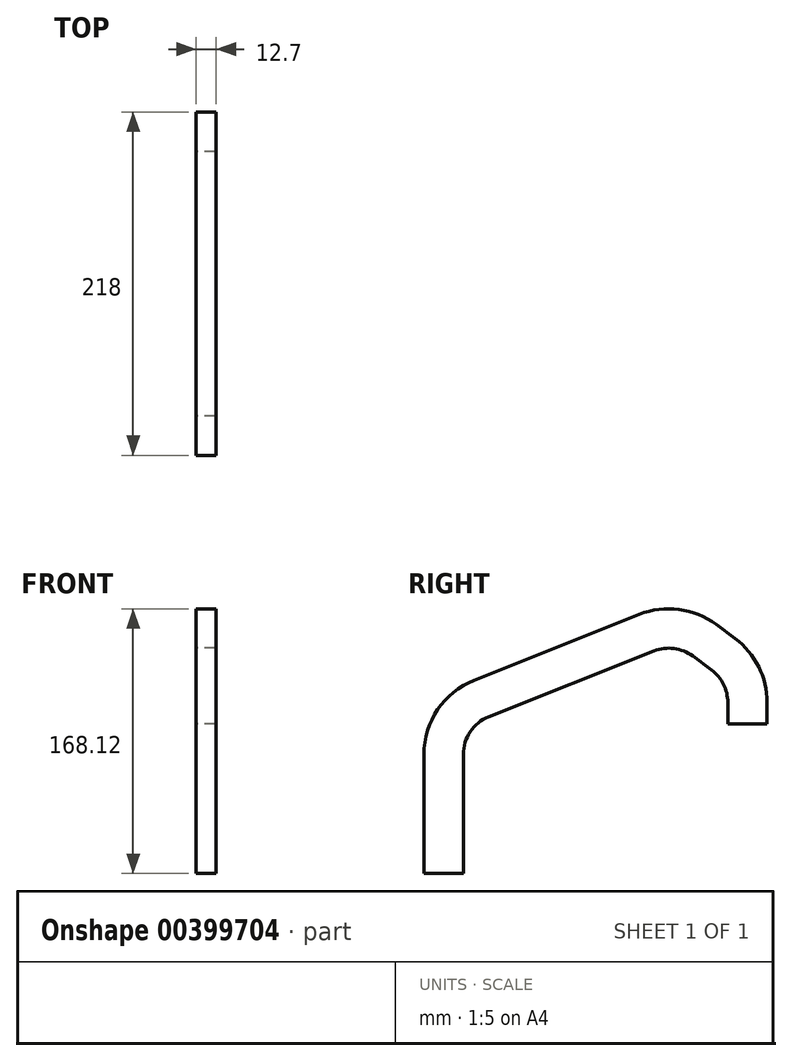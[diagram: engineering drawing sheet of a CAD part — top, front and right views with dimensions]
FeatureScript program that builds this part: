
annotation { "Feature Type Name" : "Feature", "Feature Type Description" : "" }
export const myFeature = defineFeature(function(context is Context, id is Id, definition is map)
    precondition{}
    {
        {
            var Q0;
            Q0=qCreatedBy(makeId("Right.planeOp"),FACE);
            var sketch = newSketch(context, id + "F0", { "sketchPlane" : qUnion([Q0])});
            skLineSegment(sketch, "E0", {"start": v(-159.27, -36.6) * mm, "end": v(-159.27, -146.6) * mm});
            skLineSegment(sketch, "E1", {"start": v(-159.27, -146.6) * mm, "end": v(-134.27, -146.6) * mm});
            skLineSegment(sketch, "E2", {"start": v(-134.27, -146.6) * mm, "end": v(-134.27, -53.54) * mm});
            skLineSegment(sketch, "E3", {"start": v(-134.27, -53.54) * mm, "end": v(0, 0) * mm});
            skLineSegment(sketch, "E4", {"start": v(0, 0) * mm, "end": v(33.73, -25.14) * mm});
            skLineSegment(sketch, "E5", {"start": v(33.73, -25.14) * mm, "end": v(33.73, -51.6) * mm});
            skLineSegment(sketch, "E6", {"start": v(33.73, -51.6) * mm, "end": v(58.73, -51.6) * mm});
            skLineSegment(sketch, "E7", {"start": v(58.73, -51.6) * mm, "end": v(58.73, -12.6) * mm});
            skLineSegment(sketch, "E8", {"start": v(58.73, -12.6) * mm, "end": v(3.73, 28.4) * mm});
            skLineSegment(sketch, "E9", {"start": v(3.73, 28.4) * mm, "end": v(-159.27, -36.6) * mm});
            skLineSegment(sketch, "E10", {"start": v(-159.27, -36.6) * mm, "end": v(-134.27, -53.54) * mm, "construction": true});
            skLineSegment(sketch, "E11", {"start": v(0, 0) * mm, "end": v(3.73, 28.4) * mm, "construction": true});
            skLineSegment(sketch, "E12", {"start": v(33.73, -25.14) * mm, "end": v(58.73, -12.6) * mm, "construction": true});
            skLineSegment(sketch, "E13", {"start": v(-146.77, -146.6) * mm, "end": v(-146.77, -70.9) * mm, "construction": true});
            skLineSegment(sketch, "E14", {"start": v(-122.78, -35.5) * mm, "end": v(-17.93, 6.3) * mm, "construction": true});
            skLineSegment(sketch, "E15", {"start": v(18.95, 1.46) * mm, "end": v(30.9, -7.44) * mm, "construction": true});
            skLineSegment(sketch, "E16", {"start": v(46.23, -38) * mm, "end": v(46.23, -51.6) * mm, "construction": true});
            skPoint(sketch, "E17.visualSharp", {"position": v(-146.77, -45.07) * mm});
            skArc(sketch, "E17.filletArc", {"start": v(-122.78, -35.5) * mm, "mid": v(-140.2, -49.52) * mm, "end": v(-146.77, -70.9) * mm, "construction": true});
            skPoint(sketch, "E18.visualSharp", {"position": v(1.86, 14.2) * mm});
            skArc(sketch, "E18.filletArc", {"start": v(18.95, 1.46) * mm, "mid": v(1.14, 8.7) * mm, "end": v(-17.93, 6.3) * mm, "construction": true});
            skPoint(sketch, "E19.visualSharp", {"position": v(46.23, -18.87) * mm});
            skArc(sketch, "E19.filletArc", {"start": v(46.23, -38) * mm, "mid": v(42.18, -20.9) * mm, "end": v(30.9, -7.44) * mm, "construction": true});
            skLineSegment(sketch, "E20.0", {"start": v(33.73, -38) * mm, "end": v(33.73, -51.6) * mm});
            skArc(sketch, "E20.1", {"start": v(33.73, -38) * mm, "mid": v(31.01, -26.5) * mm, "end": v(23.43, -17.47) * mm});
            skLineSegment(sketch, "E20.2", {"start": v(11.48, -8.56) * mm, "end": v(23.43, -17.47) * mm});
            skLineSegment(sketch, "E20.3", {"start": v(-134.27, -146.6) * mm, "end": v(-134.27, -70.9) * mm});
            skArc(sketch, "E20.4", {"start": v(-118.15, -47.12) * mm, "mid": v(-129.86, -56.53) * mm, "end": v(-134.27, -70.9) * mm});
            skLineSegment(sketch, "E20.5", {"start": v(-118.15, -47.12) * mm, "end": v(-13.3, -5.3) * mm});
            skArc(sketch, "E20.6", {"start": v(11.48, -8.56) * mm, "mid": v(-0.49, -3.7) * mm, "end": v(-13.3, -5.3) * mm});
            skLineSegment(sketch, "E21.0", {"start": v(58.73, -38) * mm, "end": v(58.73, -51.6) * mm});
            skArc(sketch, "E21.1", {"start": v(58.73, -38) * mm, "mid": v(53.35, -15.3) * mm, "end": v(38.37, 2.58) * mm});
            skLineSegment(sketch, "E21.2", {"start": v(26.42, 11.48) * mm, "end": v(38.37, 2.58) * mm});
            skLineSegment(sketch, "E21.3", {"start": v(-159.27, -146.6) * mm, "end": v(-159.27, -70.9) * mm});
            skArc(sketch, "E21.4", {"start": v(-127.41, -23.9) * mm, "mid": v(-150.56, -42.5) * mm, "end": v(-159.27, -70.9) * mm});
            skLineSegment(sketch, "E21.5", {"start": v(-127.41, -23.9) * mm, "end": v(-22.56, 17.92) * mm});
            skArc(sketch, "E21.6", {"start": v(26.42, 11.48) * mm, "mid": v(2.77, 21.09) * mm, "end": v(-22.56, 17.92) * mm});
            skLineSegment(sketch, "E22", {"start": v(33.73, -51.6) * mm, "end": v(33.73, -61.76) * mm});
            skLineSegment(sketch, "E23", {"start": v(58.73, -51.6) * mm, "end": v(58.73, -61.76) * mm});
            skLineSegment(sketch, "E24", {"start": v(58.73, -61.76) * mm, "end": v(33.73, -61.76) * mm});
            skSolve(sketch);
        }
        {
            var Q0;
            Q0=makeQuery(id+"F0.imprint","IMPRINT",FACE,{"disambiguationData":[TD([[makeQuery(id+"F0.imprint","IMPRINT",EDGE,{"derivedFrom":sQuery(id+"F0.wireOp",EDGE,"E1")}),1.0]])]});
            var Q1;
            {var subQ0=sQuery(id+"F0.wireOp",EDGE,"E2");Q1=makeQuery(id+"F0.imprint","IMPRINT",FACE,{"disambiguationData":[TD([[makeQuery(id+"F0.imprint","IMPRINT",EDGE,{"derivedFrom":subQ0}),-1.0]])]});}
            var Q2;
            {var subQ3=sQuery(id+"F0.wireOp",EDGE,"E20.6");Q2=makeQuery(id+"F0.imprint","IMPRINT",FACE,{"disambiguationData":[TD([[makeQuery(id+"F0.imprint","IMPRINT",EDGE,{"derivedFrom":subQ3}),-1.0]])]});}
            var Q3;
            {var subQ0=sQuery(id+"F0.wireOp",EDGE,"E5");Q3=makeQuery(id+"F0.imprint","IMPRINT",FACE,{"disambiguationData":[TD([[makeQuery(id+"F0.imprint","IMPRINT",EDGE,{"derivedFrom":subQ0}),-1.0]])]});}
            extrude(context, id + "F1", {"entities" : qUnion([Q0, Q1, Q2, Q3]), "depth" : 12.7 * mm});
        }
    });
